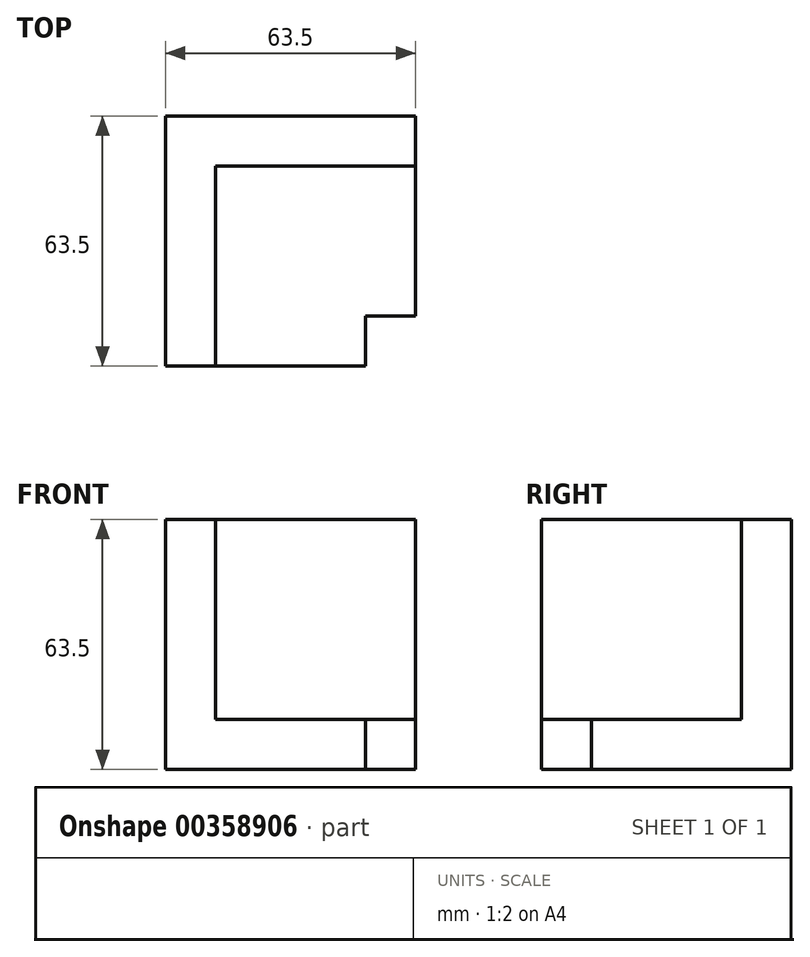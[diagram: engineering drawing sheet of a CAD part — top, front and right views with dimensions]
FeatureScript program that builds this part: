
annotation { "Feature Type Name" : "Feature", "Feature Type Description" : "" }
export const myFeature = defineFeature(function(context is Context, id is Id, definition is map)
    precondition{}
    {
        {
            var Q0;
            Q0=qCreatedBy(makeId("Front.planeOp"),FACE);
            var sketch = newSketch(context, id + "F0", { "sketchPlane" : qUnion([Q0])});
            skLineSegment(sketch, "E0.bottom", {"start": v(0, 0) * mm, "end": v(63.5, 0) * mm});
            skLineSegment(sketch, "E0.top", {"start": v(0, 63.5) * mm, "end": v(63.5, 63.5) * mm});
            skLineSegment(sketch, "E0.left", {"start": v(0, 0) * mm, "end": v(0, 63.5) * mm});
            skLineSegment(sketch, "E0.right", {"start": v(63.5, 0) * mm, "end": v(63.5, 63.5) * mm});
            skSolve(sketch);
        }
        {
            var Q0;
            Q0=qCreatedBy(makeId("Right.planeOp"),FACE);
            var sketch = newSketch(context, id + "F1", { "sketchPlane" : qUnion([Q0])});
            skLineSegment(sketch, "E1.bottom", {"start": v(0, 0) * mm, "end": v(-63.5, 0) * mm});
            skLineSegment(sketch, "E1.top", {"start": v(0, 63.5) * mm, "end": v(-63.5, 63.5) * mm});
            skLineSegment(sketch, "E1.left", {"start": v(0, 0) * mm, "end": v(0, 63.5) * mm});
            skLineSegment(sketch, "E1.right", {"start": v(-63.5, 0) * mm, "end": v(-63.5, 63.5) * mm});
            skSolve(sketch);
        }
        {
            var Q0;
            Q0=qCreatedBy(makeId("Top.planeOp"),FACE);
            var sketch = newSketch(context, id + "F2", { "sketchPlane" : qUnion([Q0])});
            skLineSegment(sketch, "E2.bottom", {"start": v(0, 0) * mm, "end": v(63.5, 0) * mm});
            skLineSegment(sketch, "E2.top", {"start": v(0, -50.8) * mm, "end": v(63.5, -50.8) * mm});
            skLineSegment(sketch, "E2.left", {"start": v(0, 0) * mm, "end": v(0, -50.8) * mm});
            skLineSegment(sketch, "E2.right", {"start": v(63.5, 0) * mm, "end": v(63.5, -50.8) * mm});
            skLineSegment(sketch, "E3.bottom", {"start": v(0, 0) * mm, "end": v(50.8, 0) * mm});
            skLineSegment(sketch, "E3.top", {"start": v(0, -63.5) * mm, "end": v(50.8, -63.5) * mm});
            skLineSegment(sketch, "E3.left", {"start": v(0, 0) * mm, "end": v(0, -63.5) * mm});
            skLineSegment(sketch, "E3.right", {"start": v(50.8, 0) * mm, "end": v(50.8, -63.5) * mm});
            skSolve(sketch);
        }
        {
            var Q0;
            Q0 = qSketchRegion(id + "F0", true);
            extrude(context, id + "F3", {"entities" : qUnion([Q0]), "depth" : 12.7 * mm});
        }
        {
            var Q0;
            Q0 = qSketchRegion(id + "F1", true);
            extrude(context, id + "F4", {"entities" : qUnion([Q0]), "operationType" : NewBodyOperationType.ADD, "depth" : 12.7 * mm});
        }
        {
            var Q0;
            Q0 = qSketchRegion(id + "F2", true);
            extrude(context, id + "F5", {"entities" : qUnion([Q0]), "operationType" : NewBodyOperationType.ADD, "depth" : 12.7 * mm});
        }
    });
